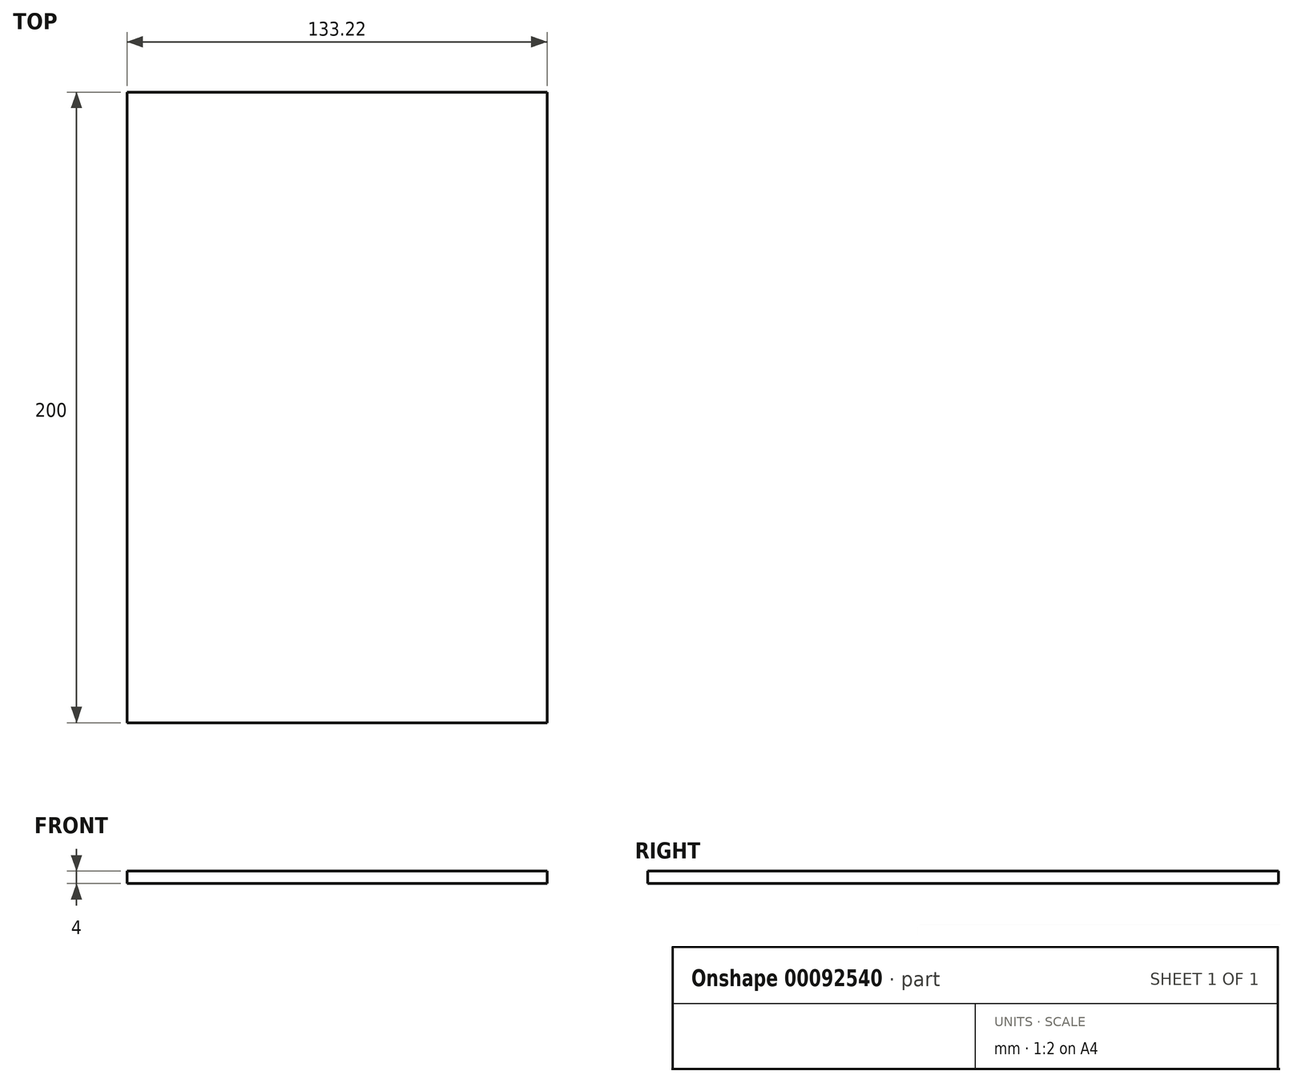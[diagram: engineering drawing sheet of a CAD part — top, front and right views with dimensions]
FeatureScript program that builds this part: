
annotation { "Feature Type Name" : "Feature", "Feature Type Description" : "" }
export const myFeature = defineFeature(function(context is Context, id is Id, definition is map)
    precondition{}
    {
        {
            var Q0;
            Q0=qCreatedBy(makeId("Top.planeOp"),FACE);
            var sketch = newSketch(context, id + "F0", { "sketchPlane" : qUnion([Q0])});
            skLineSegment(sketch, "E0.bottom", {"start": v(0, 0) * mm, "end": v(133.22, 0) * mm});
            skLineSegment(sketch, "E0.top", {"start": v(0, -200) * mm, "end": v(133.22, -200) * mm});
            skLineSegment(sketch, "E0.left", {"start": v(0, 0) * mm, "end": v(0, -200) * mm});
            skLineSegment(sketch, "E0.right", {"start": v(133.22, 0) * mm, "end": v(133.22, -200) * mm});
            skLineSegment(sketch, "E1", {"start": v(0, -22.78) * mm, "end": v(133.22, -22.78) * mm});
            skLineSegment(sketch, "E2", {"start": v(0, -170.37) * mm, "end": v(133.22, -170.37) * mm});
            skLineSegment(sketch, "E3", {"start": v(0, -170.37) * mm, "end": v(0, -200) * mm});
            skLineSegment(sketch, "E4", {"start": v(0, -22.78) * mm, "end": v(0, 0) * mm});
            skLineSegment(sketch, "E5", {"start": v(26.16, -200) * mm, "end": v(26.16, 0) * mm});
            skLineSegment(sketch, "E6", {"start": v(106.85, -200) * mm, "end": v(106.85, 0) * mm});
            skLineSegment(sketch, "E7", {"start": v(106.85, 0) * mm, "end": v(133.22, 0) * mm});
            skLineSegment(sketch, "E8", {"start": v(26.16, 0) * mm, "end": v(0, 0) * mm});
            skSolve(sketch);
        }
        {
            var Q0;
            {var subQ0=sQuery(id+"F0.wireOp",EDGE,"E0.right");var subQ1=sQuery(id+"F0.wireOp",EDGE,"E0.top");var subQ2=makeQuery(id+"F0.imprint","INTERSECT",VERTEX,{"derivedFrom":[subQ1,subQ0]});var subQ3=sQuery(id+"F0.wireOp",EDGE,"E6");var subQ10=sQuery(id+"F0.wireOp",EDGE,"E5");var subQ11=makeQuery(id+"F0.imprint","INTERSECT",VERTEX,{"derivedFrom":[subQ1,subQ10]});var subQ14=sQuery(id+"F0.wireOp",EDGE,"E0.bottom");var subQ15=makeQuery(id+"F0.imprint","INTERSECT",VERTEX,{"derivedFrom":[subQ14,subQ10]});var subQ16=sQuery(id+"F0.wireOp",EDGE,"E0.left");var subQ18=sQuery(id+"F0.wireOp",EDGE,"E1");var subQ19=makeQuery(id+"F0.imprint","INTERSECT",VERTEX,{"derivedFrom":[subQ16,subQ18]});var subQ23=makeQuery(id+"F0.imprint","INTERSECT",VERTEX,{"derivedFrom":[subQ0,subQ18]});var subQ26=makeQuery(id+"F0.imprint","INTERSECT",VERTEX,{"derivedFrom":[subQ14,subQ3]});Q0=qUnion([makeQuery(id+"F0.imprint","IMPRINT",FACE,{"disambiguationData":[TD([[makeQuery(id+"F0.imprint","IMPRINT",EDGE,{"disambiguationData":[TD([[subQ11,1.0]])],"derivedFrom":subQ1}),1.0]])]}),makeQuery(id+"F0.imprint","IMPRINT",FACE,{"disambiguationData":[TD([[makeQuery(id+"F0.imprint","IMPRINT",EDGE,{"disambiguationData":[TD([[subQ19,-1.0]])],"derivedFrom":subQ16}),1.0]])]}),makeQuery(id+"F0.imprint","IMPRINT",FACE,{"disambiguationData":[TD([[makeQuery(id+"F0.imprint","IMPRINT",EDGE,{"disambiguationData":[TD([[subQ26,-1.0]])],"derivedFrom":subQ14}),-1.0]])]}),makeQuery(id+"F0.imprint","IMPRINT",FACE,{"disambiguationData":[TD([[makeQuery(id+"F0.imprint","IMPRINT",EDGE,{"disambiguationData":[TD([[subQ15,-1.0]])],"derivedFrom":subQ14}),-1.0]])]}),makeQuery(id+"F0.imprint","IMPRINT",FACE,{"disambiguationData":[TD([[makeQuery(id+"F0.imprint","IMPRINT",EDGE,{"disambiguationData":[TD([[subQ23,-1.0]])],"derivedFrom":subQ0}),-1.0]])]}),makeQuery(id+"F0.imprint","IMPRINT",FACE,{"disambiguationData":[TD([[makeQuery(id+"F0.imprint","IMPRINT",EDGE,{"disambiguationData":[TD([[subQ15,1.0]])],"derivedFrom":subQ14}),-1.0]])]}),makeQuery(id+"F0.imprint","IMPRINT",FACE,{"disambiguationData":[TD([[makeQuery(id+"F0.imprint","IMPRINT",EDGE,{"disambiguationData":[TD([[subQ11,-1.0]])],"derivedFrom":subQ1}),1.0]])]}),makeQuery(id+"F0.imprint","IMPRINT",FACE,{"disambiguationData":[TD([[makeQuery(id+"F0.imprint","IMPRINT",EDGE,{"disambiguationData":[TD([[subQ2,1.0]])],"derivedFrom":subQ1}),1.0]])]})]);}
            var Q1;
            {var subQ0=sQuery(id+"F0.wireOp",EDGE,"E5");var subQ1=sQuery(id+"F0.wireOp",EDGE,"E1");var subQ2=makeQuery(id+"F0.imprint","INTERSECT",VERTEX,{"derivedFrom":[subQ1,subQ0]});var subQ9=sQuery(id+"F0.wireOp",EDGE,"E0.right");var subQ10=makeQuery(id+"F0.imprint","INTERSECT",VERTEX,{"derivedFrom":[subQ9,subQ1]});Q1=qUnion([makeQuery(id+"F0.imprint","IMPRINT",FACE,{"disambiguationData":[TD([[makeQuery(id+"F0.imprint","IMPRINT",EDGE,{"disambiguationData":[TD([[subQ10,-1.0]])],"derivedFrom":subQ9}),-1.0]])]}),makeQuery(id+"F0.imprint","IMPRINT",FACE,{"disambiguationData":[TD([[makeQuery(id+"F0.imprint","IMPRINT",EDGE,{"disambiguationData":[TD([[subQ2,-1.0]])],"derivedFrom":subQ1}),-1.0]])]})]);}
            extrude(context, id + "F1", {"entities" : qUnion([Q0, Q1]), "depth" : 4 * mm, "offsetDistance" : 25 * mm});
        }
    });
